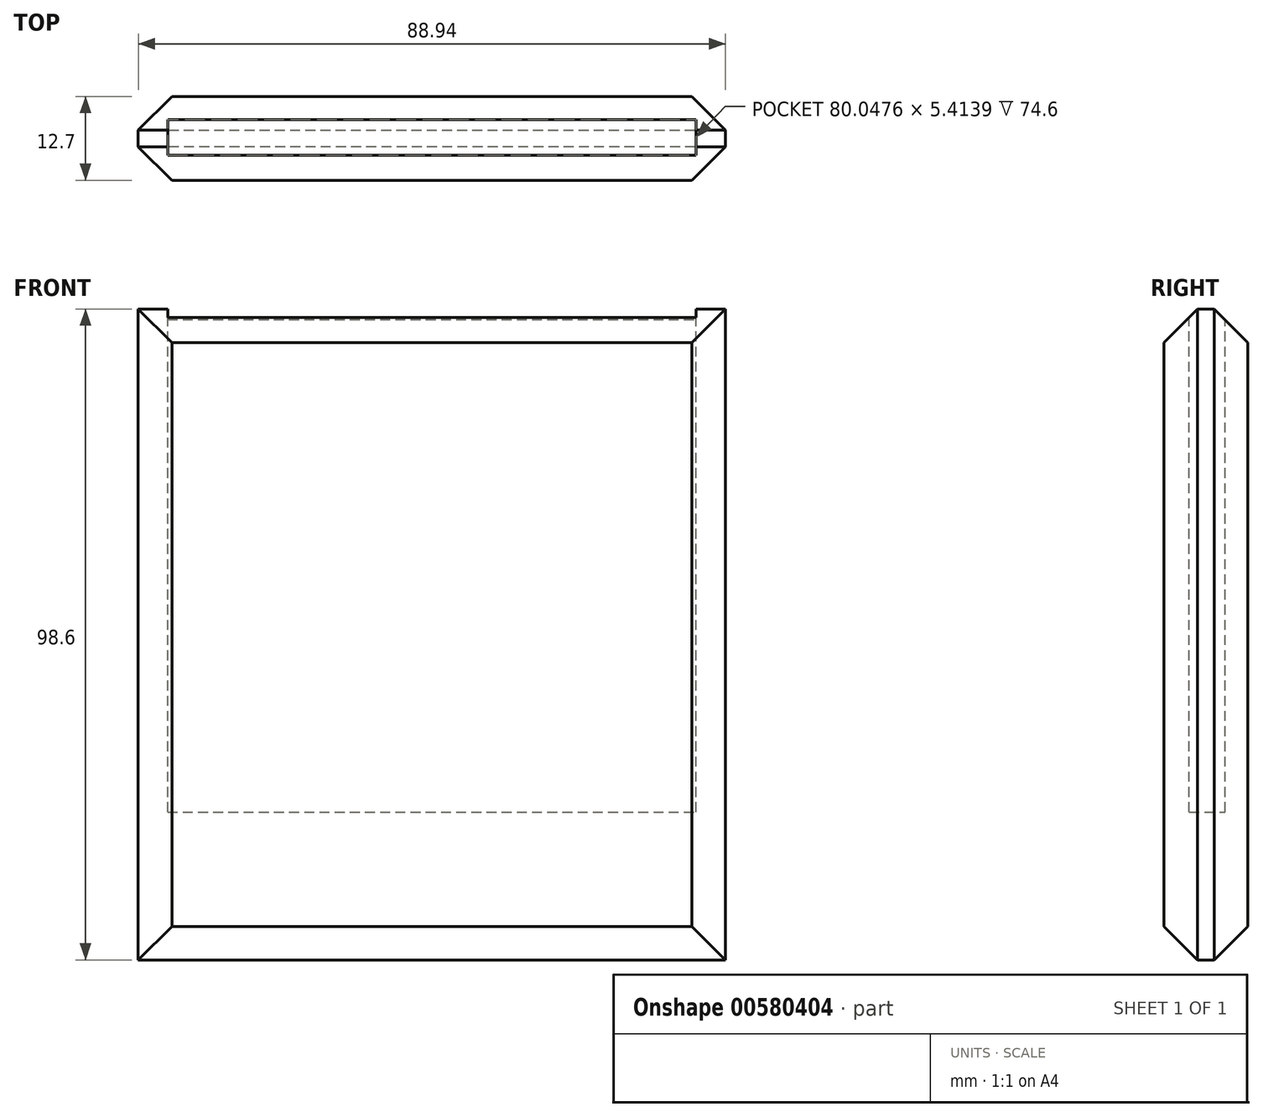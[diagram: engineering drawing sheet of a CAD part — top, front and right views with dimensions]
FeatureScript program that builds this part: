
annotation { "Feature Type Name" : "Feature", "Feature Type Description" : "" }
export const myFeature = defineFeature(function(context is Context, id is Id, definition is map)
    precondition{}
    {
        {
            var Q0;
            Q0=qCreatedBy(makeId("Front.planeOp"),FACE);
            var sketch = newSketch(context, id + "F0", { "sketchPlane" : qUnion([Q0])});
            skLineSegment(sketch, "E0.bottom", {"start": v(44.47, 49.3) * mm, "end": v(-44.47, 49.3) * mm});
            skLineSegment(sketch, "E0.top", {"start": v(44.47, -49.3) * mm, "end": v(-44.47, -49.3) * mm});
            skLineSegment(sketch, "E0.left", {"start": v(44.47, 49.3) * mm, "end": v(44.47, -49.3) * mm});
            skLineSegment(sketch, "E0.right", {"start": v(-44.47, 49.3) * mm, "end": v(-44.47, -49.3) * mm});
            skPoint(sketch, "E0.middle", {"position": v(0, 0) * mm});
            skSolve(sketch);
        }
        {
            var Q0;
            Q0=makeQuery(id+"F0.imprint","IMPRINT",FACE,{"disambiguationData":[TD([[makeQuery(id+"F0.imprint","IMPRINT",EDGE,{"derivedFrom":sQuery(id+"F0.wireOp",EDGE,"E0.bottom")}),1.0]])]});
            extrude(context, id + "F1", {"entities" : qUnion([Q0]), "depth" : 12.7 * mm, "offsetDistance" : 25.4 * mm});
        }
        {
            var Q0;
            Q0=makeQuery(id+"F1.opExtrude","SWEPT_FACE",FACE,{"disambiguationData":[OSD([sQuery(id+"F0.wireOp",EDGE,"E0.bottom")])]});
            var sketch = newSketch(context, id + "F2", { "sketchPlane" : qUnion([Q0])});
            skLineSegment(sketch, "E1.bottom", {"start": v(-40.02, -8.9) * mm, "end": v(40.02, -8.9) * mm});
            skLineSegment(sketch, "E1.top", {"start": v(-40.02, -3.48) * mm, "end": v(40.02, -3.48) * mm});
            skLineSegment(sketch, "E1.left", {"start": v(-40.02, -8.9) * mm, "end": v(-40.02, -3.48) * mm});
            skLineSegment(sketch, "E1.right", {"start": v(40.02, -8.9) * mm, "end": v(40.02, -3.48) * mm});
            skSolve(sketch);
        }
        {
            var Q0;
            Q0=makeQuery(id+"F2.imprint","IMPRINT",FACE,{"disambiguationData":[TD([[makeQuery(id+"F2.imprint","IMPRINT",EDGE,{"derivedFrom":sQuery(id+"F2.wireOp",EDGE,"E1.bottom")}),1.0]])]});
            extrude(context, id + "F3", {"entities" : qUnion([Q0]), "operationType" : NewBodyOperationType.REMOVE, "oppositeDirection" : true, "depth" : 76.2 * mm, "offsetDistance" : 25.4 * mm});
        }
        {
            var Q0;
            Q0=makeQuery(id+"F1.opExtrude","CAP_FACE",FACE,{"disambiguationData":[OSD([sQuery(id+"F0.wireOp",EDGE,"E0.bottom"),sQuery(id+"F0.wireOp",EDGE,"E0.top"),sQuery(id+"F0.wireOp",EDGE,"E0.left"),sQuery(id+"F0.wireOp",EDGE,"E0.right")])],"isStart":true});
            var Q1;
            Q1=makeQuery(id+"F1.opExtrude","CAP_FACE",FACE,{"disambiguationData":[OSD([sQuery(id+"F0.wireOp",EDGE,"E0.bottom"),sQuery(id+"F0.wireOp",EDGE,"E0.top"),sQuery(id+"F0.wireOp",EDGE,"E0.left"),sQuery(id+"F0.wireOp",EDGE,"E0.right")])],"isStart":false});
            chamfer(context, id + "F4", {"entities" : qUnion([Q0, Q1]), "width" : 5.08 * mm, "tangentPropagation" : true});
        }
    });
